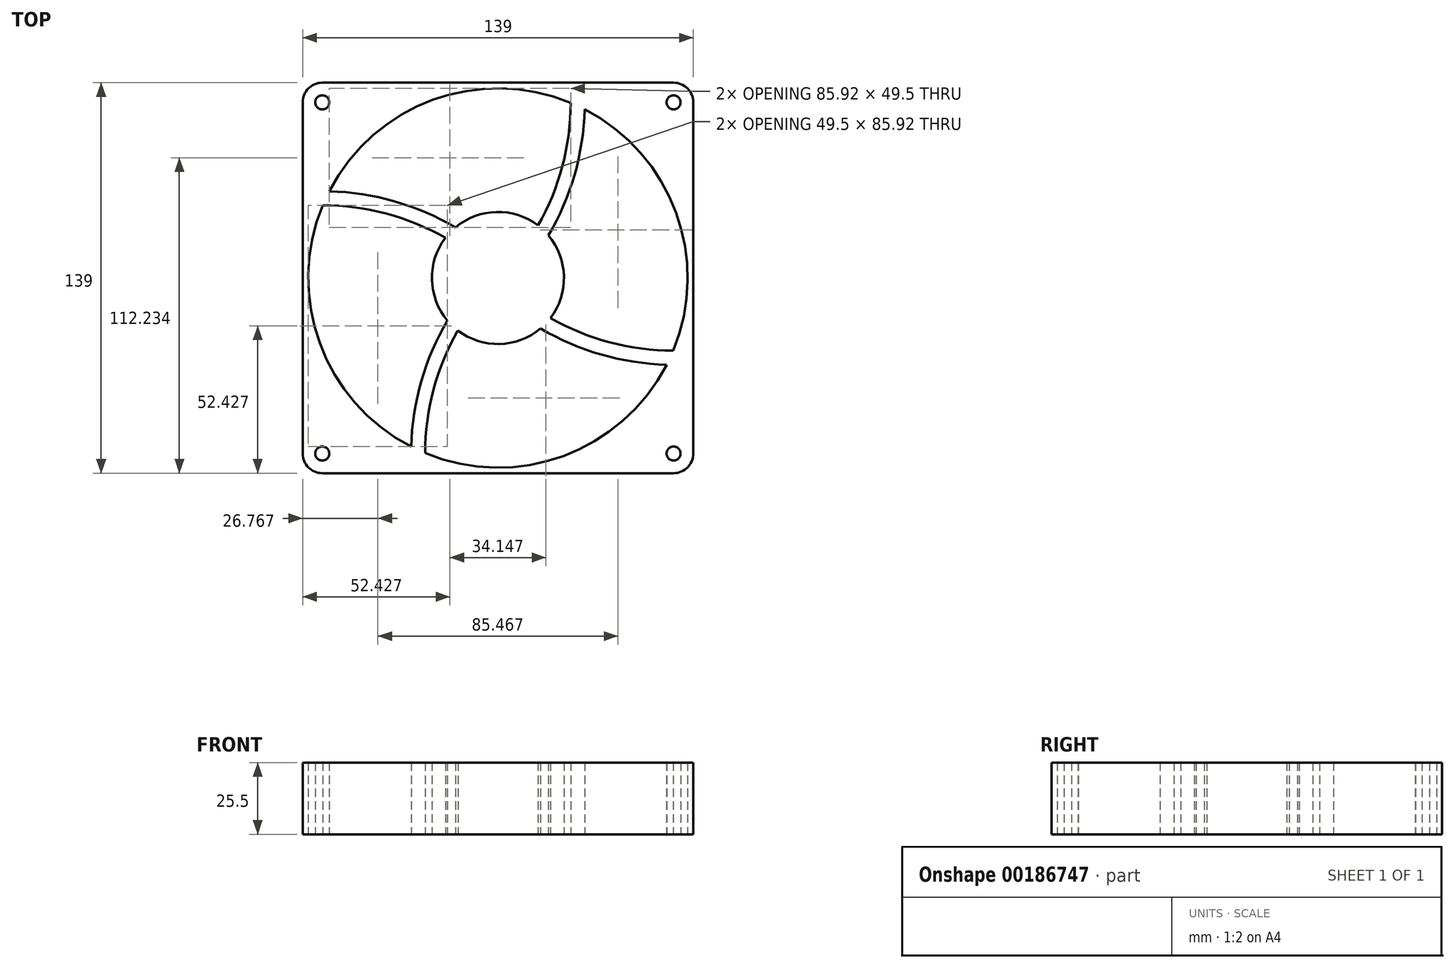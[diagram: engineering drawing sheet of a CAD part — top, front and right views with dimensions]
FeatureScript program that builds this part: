
annotation { "Feature Type Name" : "Feature", "Feature Type Description" : "" }
export const myFeature = defineFeature(function(context is Context, id is Id, definition is map)
    precondition{}
    {
        {
            var Q0;
            Q0=qCreatedBy(makeId("Top.planeOp"),FACE);
            var sketch = newSketch(context, id + "F0", { "sketchPlane" : qUnion([Q0])});
            skLineSegment(sketch, "E0", {"start": v(7, 0) * mm, "end": v(132, 0) * mm});
            skLineSegment(sketch, "E1", {"start": v(139, 7) * mm, "end": v(139, 132) * mm});
            skLineSegment(sketch, "E2", {"start": v(139, 139) * mm, "end": v(0, 139) * mm});
            skLineSegment(sketch, "E3", {"start": v(0, 132) * mm, "end": v(0, 7) * mm});
            skLineSegment(sketch, "E4", {"start": v(7, 139) * mm, "end": v(7, 139) * mm});
            skLineSegment(sketch, "E5", {"start": v(7, 139) * mm, "end": v(132, 139) * mm});
            skLineSegment(sketch, "E6", {"start": v(132, 139) * mm, "end": v(132, 139) * mm});
            skLineSegment(sketch, "E7.0", {"start": v(7, 139) * mm, "end": v(7, 0) * mm, "construction": true});
            skLineSegment(sketch, "E8.0", {"start": v(132, 0) * mm, "end": v(132, 139) * mm, "construction": true});
            skLineSegment(sketch, "E9.0", {"start": v(0, 7) * mm, "end": v(139, 7) * mm, "construction": true});
            skLineSegment(sketch, "E10.0", {"start": v(7, 132) * mm, "end": v(132, 132) * mm, "construction": true});
            skCircle(sketch, "E11", {"center": v(7, 132) * mm, "radius": 2.5 * mm});
            skCircle(sketch, "E12", {"center": v(132, 132) * mm, "radius": 2.5 * mm});
            skCircle(sketch, "E13", {"center": v(132, 7) * mm, "radius": 2.5 * mm});
            skCircle(sketch, "E14", {"center": v(7, 7) * mm, "radius": 2.5 * mm});
            skPoint(sketch, "E15.visualSharp", {"position": v(0, 139) * mm});
            skArc(sketch, "E15.filletArc", {"start": v(7, 139) * mm, "mid": v(2.05, 136.95) * mm, "end": v(0, 132) * mm});
            skPoint(sketch, "E16.visualSharp", {"position": v(139, 139) * mm});
            skArc(sketch, "E16.filletArc", {"start": v(139, 132) * mm, "mid": v(136.95, 136.95) * mm, "end": v(132, 139) * mm});
            skPoint(sketch, "E17.visualSharp", {"position": v(139, 0) * mm});
            skArc(sketch, "E17.filletArc", {"start": v(132, 0) * mm, "mid": v(136.95, 2.05) * mm, "end": v(139, 7) * mm});
            skPoint(sketch, "E18.visualSharp", {"position": v(0, 0) * mm});
            skArc(sketch, "E18.filletArc", {"start": v(0, 7) * mm, "mid": v(2.05, 2.05) * mm, "end": v(7, 0) * mm});
            skArc(sketch, "E19", {"start": v(95.39, 131.84) * mm, "mid": v(46.28, 132.88) * mm, "end": v(9.47, 100.36) * mm});
            skPoint(sketch, "E19.centerSnap0", {"position": v(0, 69.5) * mm});
            skPoint(sketch, "E19.centerSnap1", {"position": v(69.5, 139) * mm});
            skArc(sketch, "E20", {"start": v(83.76, 88.18) * mm, "mid": v(68.94, 93) * mm, "end": v(54.37, 87.48) * mm});
            skArc(sketch, "E21", {"start": v(55.24, 50.82) * mm, "mid": v(46.59, 29.75) * mm, "end": v(43.61, 7.16) * mm});
            skArc(sketch, "E22.0", {"start": v(84.63, 51.52) * mm, "mid": v(106.26, 42.23) * mm, "end": v(129.53, 38.64) * mm});
            skArc(sketch, "E23.0", {"start": v(51.52, 54.37) * mm, "mid": v(42.23, 32.74) * mm, "end": v(38.64, 9.47) * mm});
            skArc(sketch, "E24.trimOffspring", {"start": v(83.76, 88.18) * mm, "mid": v(92.41, 109.25) * mm, "end": v(95.39, 131.84) * mm});
            skArc(sketch, "E25.trimOffspring", {"start": v(87.48, 84.63) * mm, "mid": v(96.77, 106.26) * mm, "end": v(100.36, 129.53) * mm});
            skArc(sketch, "E26.trimOffspring", {"start": v(88.18, 55.24) * mm, "mid": v(93, 70.06) * mm, "end": v(87.48, 84.63) * mm});
            skArc(sketch, "E27.trimOffspring", {"start": v(131.84, 43.61) * mm, "mid": v(132.88, 92.72) * mm, "end": v(100.36, 129.53) * mm});
            skArc(sketch, "E28.trimOffspring", {"start": v(55.24, 50.82) * mm, "mid": v(70.06, 46) * mm, "end": v(84.63, 51.52) * mm});
            skArc(sketch, "E29.trimOffspring", {"start": v(43.61, 7.16) * mm, "mid": v(92.72, 6.12) * mm, "end": v(129.53, 38.64) * mm});
            skArc(sketch, "E30.trimOffspring", {"start": v(7.16, 95.39) * mm, "mid": v(6.12, 46.28) * mm, "end": v(38.64, 9.47) * mm});
            skArc(sketch, "E31.trimOffspring", {"start": v(50.82, 83.76) * mm, "mid": v(29.75, 92.41) * mm, "end": v(7.16, 95.39) * mm});
            skArc(sketch, "E32.trimOffspring", {"start": v(50.82, 83.76) * mm, "mid": v(46, 68.94) * mm, "end": v(51.52, 54.37) * mm});
            skArc(sketch, "E33.trimOffspring", {"start": v(54.37, 87.48) * mm, "mid": v(32.74, 96.77) * mm, "end": v(9.47, 100.36) * mm});
            skArc(sketch, "E34.trimOffspring", {"start": v(88.18, 55.24) * mm, "mid": v(109.25, 46.59) * mm, "end": v(131.84, 43.61) * mm});
            skSolve(sketch);
        }
        {
            var Q0;
            Q0=makeQuery(id+"F0.imprint","IMPRINT",FACE,{"disambiguationData":[TD([[makeQuery(id+"F0.imprint","IMPRINT",EDGE,{"derivedFrom":sQuery(id+"F0.wireOp",EDGE,"E0")}),1.0]])]});
            var Q1;
            Q1=makeQuery(id+"F0.imprint","IMPRINT",FACE,{"disambiguationData":[TD([[makeQuery(id+"F0.imprint","IMPRINT",EDGE,{"derivedFrom":sQuery(id+"F0.wireOp",EDGE,"E20")}),1.0]])]});
            extrude(context, id + "F1", {"entities" : qUnion([Q0, Q1]), "depth" : 25.5 * mm});
        }
    });
